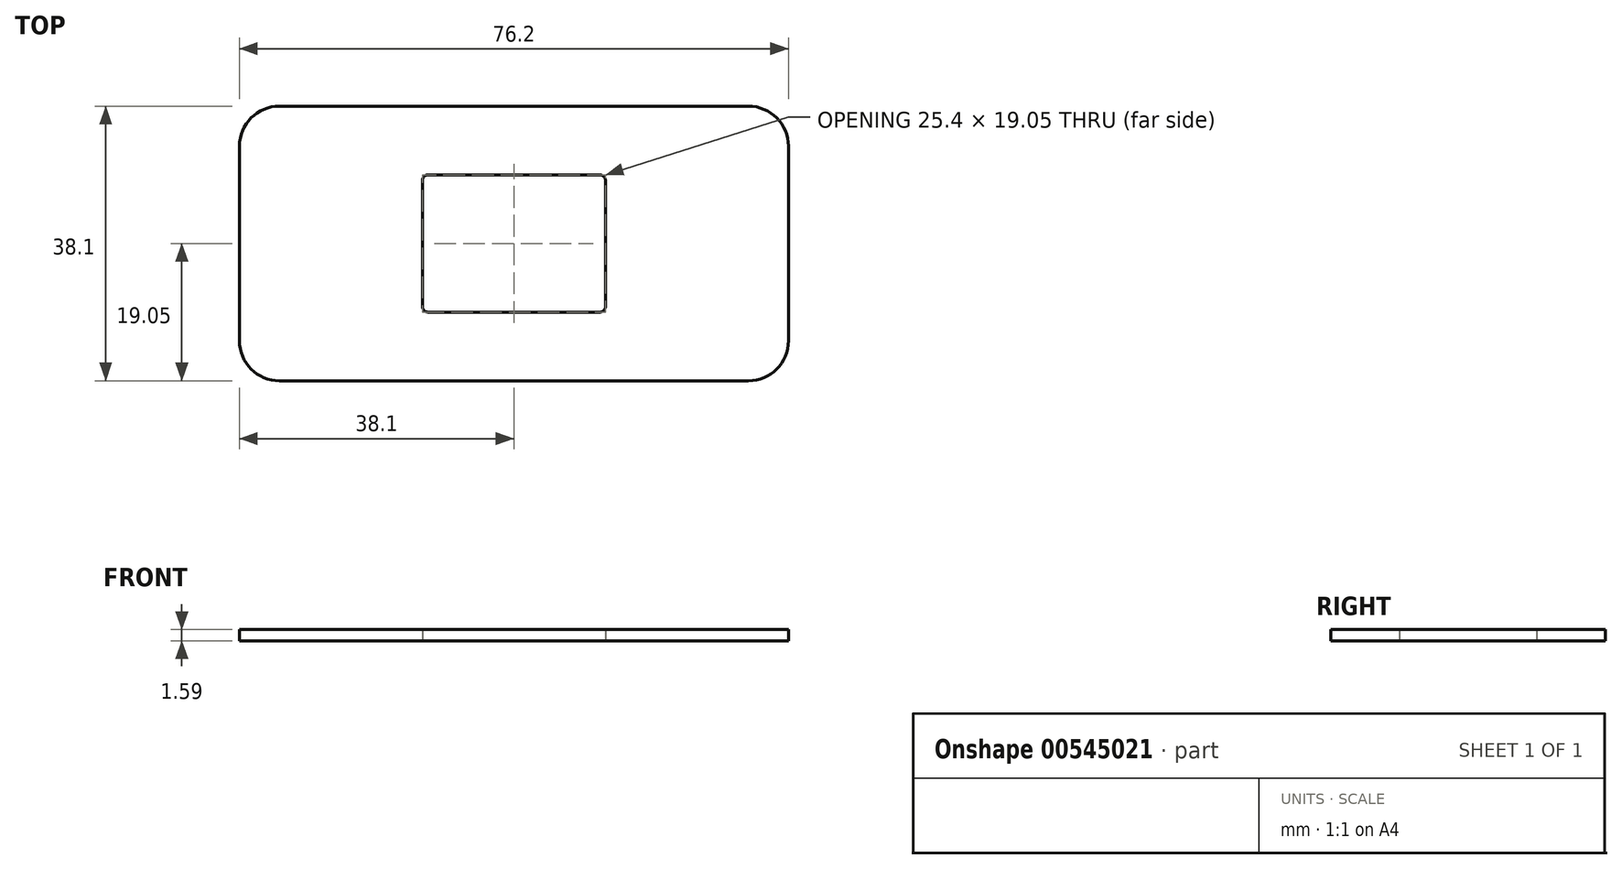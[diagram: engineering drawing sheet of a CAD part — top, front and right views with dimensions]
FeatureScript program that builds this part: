
annotation { "Feature Type Name" : "Feature", "Feature Type Description" : "" }
export const myFeature = defineFeature(function(context is Context, id is Id, definition is map)
    precondition{}
    {
        {
            var Q0;
            Q0=qCreatedBy(makeId("Top.planeOp"),FACE);
            var sketch = newSketch(context, id + "F0", { "sketchPlane" : qUnion([Q0])});
            skLineSegment(sketch, "E0.bottom", {"start": v(5.56, 0) * mm, "end": v(70.64, 0) * mm});
            skLineSegment(sketch, "E0.top", {"start": v(5.56, 38.1) * mm, "end": v(70.64, 38.1) * mm});
            skLineSegment(sketch, "E0.left", {"start": v(0, 5.56) * mm, "end": v(0, 32.54) * mm});
            skLineSegment(sketch, "E0.right", {"start": v(76.2, 5.56) * mm, "end": v(76.2, 32.54) * mm});
            skLineSegment(sketch, "E1.bottom", {"start": v(26.2, 28.58) * mm, "end": v(50, 28.58) * mm});
            skLineSegment(sketch, "E1.top", {"start": v(26.2, 9.53) * mm, "end": v(50, 9.53) * mm});
            skLineSegment(sketch, "E1.left", {"start": v(25.4, 27.78) * mm, "end": v(25.4, 10.32) * mm});
            skLineSegment(sketch, "E1.right", {"start": v(50.8, 27.78) * mm, "end": v(50.8, 10.32) * mm});
            skLineSegment(sketch, "E2", {"start": v(50.8, 28.58) * mm, "end": v(25.4, 9.53) * mm, "construction": true});
            skLineSegment(sketch, "E3", {"start": v(0, 38.1) * mm, "end": v(76.2, 0) * mm, "construction": true});
            skPoint(sketch, "E4", {"position": v(38.1, 19.05) * mm});
            skPoint(sketch, "E5.visualSharp", {"position": v(0, 38.1) * mm});
            skArc(sketch, "E5.filletArc", {"start": v(5.56, 38.1) * mm, "mid": v(1.63, 36.47) * mm, "end": v(0, 32.54) * mm});
            skPoint(sketch, "E6.visualSharp", {"position": v(0, 0) * mm});
            skArc(sketch, "E6.filletArc", {"start": v(0, 5.56) * mm, "mid": v(1.63, 1.63) * mm, "end": v(5.56, 0) * mm});
            skPoint(sketch, "E7.visualSharp", {"position": v(76.2, 0) * mm});
            skArc(sketch, "E7.filletArc", {"start": v(70.64, 0) * mm, "mid": v(74.57, 1.63) * mm, "end": v(76.2, 5.56) * mm});
            skPoint(sketch, "E8.visualSharp", {"position": v(76.2, 38.1) * mm});
            skArc(sketch, "E8.filletArc", {"start": v(76.2, 32.54) * mm, "mid": v(74.57, 36.47) * mm, "end": v(70.64, 38.1) * mm});
            skPoint(sketch, "E9.visualSharp", {"position": v(25.4, 28.58) * mm});
            skArc(sketch, "E9.filletArc", {"start": v(26.2, 28.58) * mm, "mid": v(25.63, 28.34) * mm, "end": v(25.4, 27.78) * mm});
            skPoint(sketch, "E10.visualSharp", {"position": v(50.8, 28.58) * mm});
            skArc(sketch, "E10.filletArc", {"start": v(50.8, 27.78) * mm, "mid": v(50.57, 28.34) * mm, "end": v(50, 28.58) * mm});
            skPoint(sketch, "E11.visualSharp", {"position": v(50.8, 9.53) * mm});
            skArc(sketch, "E11.filletArc", {"start": v(50, 9.53) * mm, "mid": v(50.57, 9.76) * mm, "end": v(50.8, 10.32) * mm});
            skPoint(sketch, "E12.visualSharp", {"position": v(25.4, 9.53) * mm});
            skArc(sketch, "E12.filletArc", {"start": v(25.4, 10.32) * mm, "mid": v(25.63, 9.76) * mm, "end": v(26.2, 9.53) * mm});
            skSolve(sketch);
        }
        {
            var Q0;
            Q0=makeQuery(id+"F0.imprint","IMPRINT",FACE,{"disambiguationData":[TD([[makeQuery(id+"F0.imprint","IMPRINT",EDGE,{"derivedFrom":sQuery(id+"F0.wireOp",EDGE,"E0.bottom")}),1.0]])]});
            extrude(context, id + "F1", {"entities" : qUnion([Q0]), "depth" : 1.59 * mm, "offsetDistance" : 25.4 * mm});
        }
    });
